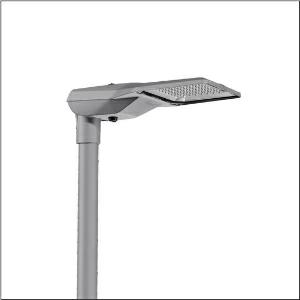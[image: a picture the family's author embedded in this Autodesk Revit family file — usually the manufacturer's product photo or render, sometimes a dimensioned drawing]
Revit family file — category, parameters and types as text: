
# Revit family: streetlight_sl_21_iq_midi___st1_0a_5xe3d41y08nb_87cf
name_source: partatom
category: Lighting Fixtures
units: mm (PartAtom-declared; Revit-internal decimal feet)

## family parameters
Cut with Voids When Loaded = No
Host = Face
Light Source = No
Part Type = Normal
Room Calculation Point = No
Round Connector Dimension = Use Diameter
Shared = No

## types (1)
- --- (1 x LED, 22330 lm, 136.6 W, 4000K)
    Apparent Load = 137 VA
    CIE Flux Codes = 40 73 97 100 100
    Color Rendering = 70
    Color Temperature = 4000K
    Default Elevation = 1800 mm
    Description = Streetlight SL 21 iQ midi, mast luminaire, primary light control with lens, of PMMA, primary optical cover: cover, of toughened safety glass, transparent, light distribution: ST1.0a, light emission: direct distribution, primary light characteristic: asymmetric, installation type: post-top, side-entry, LED, High Power LED, rated luminous flux: 22.330lm, luminous efficacy: 164lm/W, light colour: 740, colour temperature: 4000K, control: presetting dimming logarithmic, Street-Remote, Auto-Match, Temp-Guard, Lumen-Switch, Night-Set, Smart-Wire, Light-Fading, Desk-Remote (wireless, voltage-free reading and setting of iQ features in the workshop via application-optimized NFC function/RFID function), optimised constant luminous flux control (CLO 2.0), mains connection: 230..240V, AC, 50/60Hz, start of lifetime: 137W, end of service life: 144W, reduction: 62W, luminaire housing, of diecast aluminium, powder-coated, Siteco® metallic grey (DB 702S), corrosivity category C5 mid according to DIN EN ISO 12944, please order mast flange separately, inclination adjustable: 0°, 5°, 10°, 15°, sealing non-destructively replaceable, multi-level sealing system, length: 644mm, width: 335mm, height: 110mm, mast flange for spigot size: 42mm (side-entry): 5XC10008XM4, 60/48mm (side-entry/post-top): 5XC10108XM2, 76/60mm (side-entry/post-top): 5XC10108XM1, Smart Interface below and above, protection rating (complete): IP66, insulation class (complete): insulation class II (safety insulation), certification: CE, ENEC, ENEC+, VDE, impact resistance: IK09, permissible operating ambient temperature for outdoor applications: -40..+50°C, standard-compliant lighting for roads and squares, packaging unit: 1 piece

Light Distribution: ST1.0a
    Height = 111 mm
    Lamp = 1 x LED
    Lamp Light Flux = 22330 lm
    Lamp Power = 136.6 W
    Lamp count = 1
    Length = 644 mm
    Luminous efficacy = 163 lm/W
    Manufacturer = Siteco
    ModVariant = No
    Model = 5XE3D41Y08NB
    Number of Poles = 1
    OnlyDefault = Yes
    Power Factor = 1
    Product Name = Streetlight SL 21 iQ midi | ST1.0a
    Product group = mast luminaire | pylon top
    ProductGroupID = 6100
    Protection Class = Protection class II
    Protection Degree = IP 66
    RLX_Detail_Level = 1
    RLX_Emergency_Light_Flux = 0 lm
    RLX_Emergency_Type = 0
    RLX_Emergency_Type_DB = No
    RlxData = <blob elided: 91165 chars, md5=368dd33a>
    Socket = socket
    Standby Power = 0 W
    System Light Flux = 22330 lm
    System Power = 137 W
    Type Comments = factory setting: luminous flux: 100 % | dim-lin: 254 | 733 mA
    Type Image = l_1004304.jpg
    URL = http://relux.com
    VarID = @adj_043769
    Voltage = 0 V
    Weight = 0.00 kg
    Width = 336 mm

## geometry (parser evidence)
native form markers: Blend x4, Sweep x12
no freeform markers — native parametric forms only
